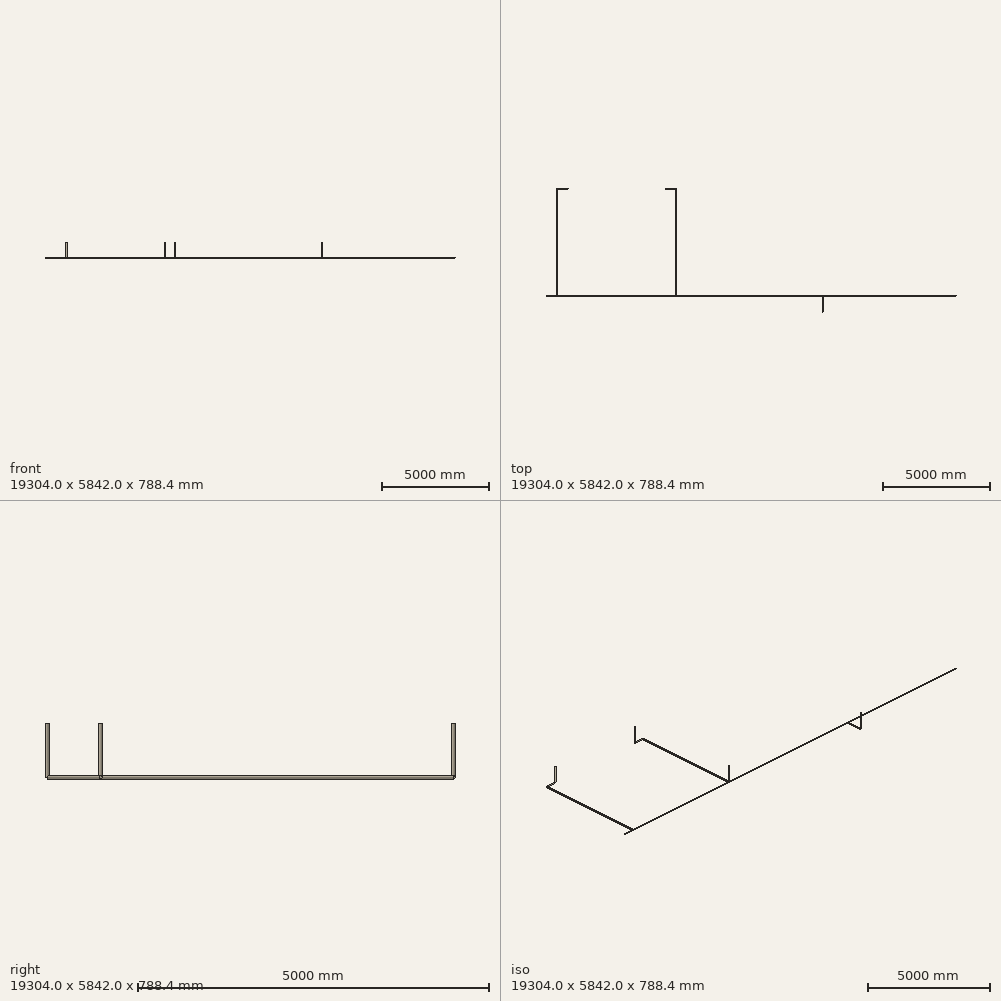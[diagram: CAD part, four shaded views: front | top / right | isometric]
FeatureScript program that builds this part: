
annotation { "Feature Type Name" : "Feature", "Feature Type Description" : "" }
export const myFeature = defineFeature(function(context is Context, id is Id, definition is map)
    precondition{}
    {
        {
            var Q0;
            Q0=qCreatedBy(makeId("Right.planeOp"),FACE);
            var sketch = newSketch(context, id + "F0", { "sketchPlane" : qUnion([Q0])});
            skCircle(sketch, "E0", {"center": v(0, 0) * mm, "radius": 25.4 * mm});
            skSolve(sketch);
        }
        {
            var Q0;
            Q0 = qSketchRegion(id + "F0", true);
            extrude(context, id + "F1", {"entities" : qUnion([Q0]), "oppositeDirection" : true, "depth" : 6096 * mm, "offsetDistance" : 25.4 * mm});
        }
        {
            var Q0;
            Q0=qCreatedBy(makeId("Top.planeOp"),FACE);
            var sketch = newSketch(context, id + "F2", { "sketchPlane" : qUnion([Q0])});
            skCircle(sketch, "E1", {"center": v(0, 0) * mm, "radius": 25.4 * mm});
            skSolve(sketch);
        }
        {
            var Q0;
            Q0 = qSketchRegion(id + "F2", true);
            extrude(context, id + "F3", {"entities" : qUnion([Q0]), "operationType" : NewBodyOperationType.ADD, "depth" : 762 * mm, "offsetDistance" : 25.4 * mm});
        }
        {
            var Q0;
            Q0=qCreatedBy(makeId("Front.planeOp"),FACE);
            var sketch = newSketch(context, id + "F4", { "sketchPlane" : qUnion([Q0])});
            skCircle(sketch, "E2", {"center": v(0, -1.02) * mm, "radius": 25.4 * mm});
            skSolve(sketch);
        }
        {
            var Q0;
            Q0 = qSketchRegion(id + "F4", true);
            extrude(context, id + "F5", {"entities" : qUnion([Q0]), "operationType" : NewBodyOperationType.ADD, "oppositeDirection" : true, "depth" : 5029.2 * mm, "offsetDistance" : 25.4 * mm});
        }
        {
            var Q0;
            Q0=makeQuery(id+"F5.opExtrude","CAP_FACE",FACE,{"disambiguationData":[OSD([sQuery(id+"F4.wireOp",EDGE,"E2")])],"isStart":false});
            var sketch = newSketch(context, id + "F6", { "sketchPlane" : qUnion([Q0])});
            skPoint(sketch, "E3", {"position": v(0, 0) * mm});
            skSolve(sketch);
        }
        {
            var Q0;
            Q0=qCreatedBy(makeId("Right.planeOp"),FACE);
            var sketch = newSketch(context, id + "F7", { "sketchPlane" : qUnion([Q0])});
            skCircle(sketch, "E4", {"center": v(5029.2, 0) * mm, "radius": 25.4 * mm});
            skSolve(sketch);
        }
        {
            var Q0;
            Q0 = qSketchRegion(id + "F7", true);
            extrude(context, id + "F8", {"entities" : qUnion([Q0]), "operationType" : NewBodyOperationType.ADD, "oppositeDirection" : true, "depth" : 457.2 * mm, "offsetDistance" : 25.4 * mm});
        }
        {
            var Q0;
            Q0=makeQuery(id+"F8.opExtrude","CAP_FACE",FACE,{"disambiguationData":[OSD([sQuery(id+"F7.wireOp",EDGE,"E4")])],"isStart":false});
            var sketch = newSketch(context, id + "F9", { "sketchPlane" : qUnion([Q0])});
            skPoint(sketch, "E5", {"position": v(-5029.2, 0) * mm});
            skSolve(sketch);
        }
        {
            var Q0;
            Q0=qCreatedBy(makeId("Top.planeOp"),FACE);
            var sketch = newSketch(context, id + "F10", { "sketchPlane" : qUnion([Q0])});
            skCircle(sketch, "E6", {"center": v(-457.2, 5029.2) * mm, "radius": 25.4 * mm});
            skSolve(sketch);
        }
        {
            var Q0;
            Q0 = qSketchRegion(id + "F10", true);
            extrude(context, id + "F11", {"entities" : qUnion([Q0]), "operationType" : NewBodyOperationType.ADD, "depth" : 762 * mm, "offsetDistance" : 25.4 * mm});
        }
        {
            var Q0;
            Q0=qCreatedBy(makeId("Front.planeOp"),FACE);
            var sketch = newSketch(context, id + "F12", { "sketchPlane" : qUnion([Q0])});
            skCircle(sketch, "E7", {"center": v(-5600.7, 0) * mm, "radius": 25.4 * mm});
            skSolve(sketch);
        }
        {
            var Q0;
            Q0 = qSketchRegion(id + "F12", true);
            extrude(context, id + "F13", {"entities" : qUnion([Q0]), "operationType" : NewBodyOperationType.ADD, "oppositeDirection" : true, "depth" : 5029.2 * mm, "offsetDistance" : 25.4 * mm});
        }
        {
            var Q0;
            Q0=makeQuery(id+"F13.opExtrude","CAP_FACE",FACE,{"disambiguationData":[OSD([sQuery(id+"F12.wireOp",EDGE,"E7")])],"isStart":false});
            var sketch = newSketch(context, id + "F14", { "sketchPlane" : qUnion([Q0])});
            skPoint(sketch, "E8", {"position": v(5600.7, 0) * mm});
            skSolve(sketch);
        }
        {
            var Q0;
            Q0=sQuery(id+"F14.wireOp",VERTEX,"E8");
            var Q1;
            Q1=qCreatedBy(makeId("Right.planeOp"),FACE);
            cPlane(context, id + "F15", {"entities" : qUnion([Q0, Q1]), "cplaneType" : CPlaneType.PLANE_POINT, "offset" : 25.4 * mm, "width" : 152.4 * mm, "height" : 152.4 * mm});
        }
        {
            var Q0;
            Q0=qCreatedBy(id+"F15.planeOp",FACE);
            var sketch = newSketch(context, id + "F16", { "sketchPlane" : qUnion([Q0])});
            skCircle(sketch, "E9", {"center": v(5029.2, 0) * mm, "radius": 25.4 * mm});
            skSolve(sketch);
        }
        {
            var Q0;
            Q0 = qSketchRegion(id + "F16", true);
            extrude(context, id + "F17", {"entities" : qUnion([Q0]), "operationType" : NewBodyOperationType.ADD, "depth" : 495.3 * mm, "offsetDistance" : 25.4 * mm});
        }
        {
            var Q0;
            Q0=makeQuery(id+"F17.opExtrude","CAP_FACE",FACE,{"disambiguationData":[OSD([sQuery(id+"F16.wireOp",EDGE,"E9")])],"isStart":false});
            var sketch = newSketch(context, id + "F18", { "sketchPlane" : qUnion([Q0])});
            skPoint(sketch, "E10", {"position": v(5029.2, 0) * mm});
            skSolve(sketch);
        }
        {
            var Q0;
            Q0=qCreatedBy(makeId("Top.planeOp"),FACE);
            var sketch = newSketch(context, id + "F19", { "sketchPlane" : qUnion([Q0])});
            skCircle(sketch, "E11", {"center": v(-5105.4, 5029.2) * mm, "radius": 25.4 * mm});
            skSolve(sketch);
        }
        {
            var Q0;
            Q0 = qSketchRegion(id + "F19", true);
            extrude(context, id + "F20", {"entities" : qUnion([Q0]), "operationType" : NewBodyOperationType.ADD, "depth" : 762 * mm, "offsetDistance" : 25.4 * mm});
        }
        {
            var Q0;
            Q0=qCreatedBy(makeId("Right.planeOp"),FACE);
            var sketch = newSketch(context, id + "F21", { "sketchPlane" : qUnion([Q0])});
            skCircle(sketch, "E12", {"center": v(0, 0) * mm, "radius": 25.4 * mm});
            skSolve(sketch);
        }
        {
            var Q0;
            Q0 = qSketchRegion(id + "F21", true);
            extrude(context, id + "F22", {"entities" : qUnion([Q0]), "operationType" : NewBodyOperationType.ADD, "depth" : 13208 * mm, "offsetDistance" : 25.4 * mm});
        }
        {
            var Q0;
            Q0=qCreatedBy(makeId("Front.planeOp"),FACE);
            var sketch = newSketch(context, id + "F23", { "sketchPlane" : qUnion([Q0])});
            skCircle(sketch, "E13", {"center": v(6908.8, 0) * mm, "radius": 25.4 * mm});
            skSolve(sketch);
        }
        {
            var Q0;
            Q0 = qSketchRegion(id + "F23", true);
            extrude(context, id + "F24", {"entities" : qUnion([Q0]), "operationType" : NewBodyOperationType.ADD, "depth" : 762 * mm, "offsetDistance" : 25.4 * mm});
        }
        {
            var Q0;
            Q0=makeQuery(id+"F24.opExtrude","CAP_FACE",FACE,{"disambiguationData":[OSD([sQuery(id+"F23.wireOp",EDGE,"E13")])],"isStart":false});
            var sketch = newSketch(context, id + "F25", { "sketchPlane" : qUnion([Q0])});
            skPoint(sketch, "E14", {"position": v(6908.8, 0) * mm});
            skSolve(sketch);
        }
        {
            var Q0;
            Q0=qCreatedBy(makeId("Top.planeOp"),FACE);
            var sketch = newSketch(context, id + "F26", { "sketchPlane" : qUnion([Q0])});
            skCircle(sketch, "E15", {"center": v(6908.8, -762) * mm, "radius": 25.4 * mm});
            skSolve(sketch);
        }
        {
            var Q0;
            Q0 = qSketchRegion(id + "F26", true);
            extrude(context, id + "F27", {"entities" : qUnion([Q0]), "operationType" : NewBodyOperationType.ADD, "depth" : 762 * mm, "offsetDistance" : 25.4 * mm});
        }
    });
